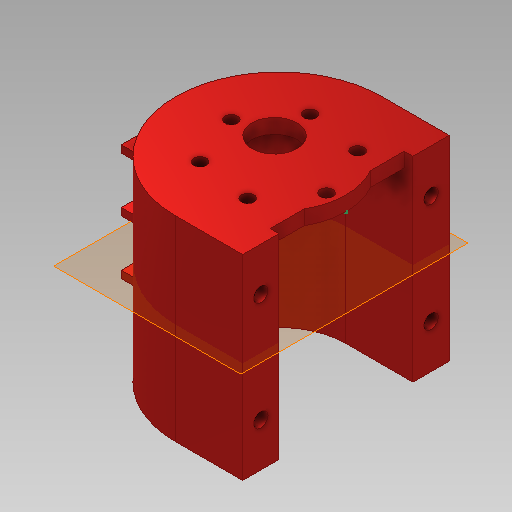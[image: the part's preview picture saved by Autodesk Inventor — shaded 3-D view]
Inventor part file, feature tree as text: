
AUTODESK INVENTOR PART (.ipt)
format: ipt  version: 2020 (Build 240168000, 168)  size: 282,624 bytes
history: native  units: in
note: dims shown in document units (in); Inventor stores cm internally (conversion verified against a paired STEP export)
features: sketch x5, extrude x4, pattern_linear x2, plane x1, mirror x1
ambient origin geometry x8: Origin, YZ Plane, XZ Plane, XY Plane, X Axis, Y Axis, Z Axis, Center Point
bodies: Solid1 (feature_tree)
feature tree (13):
  sketch  "Sketch1"  dims[d2=0.4882in d4=0.2362in]
  extrude  "Extrusion1"  Depth=0.2362in
  extrude  "Extrusion2"  Depth=0.2756in
  sketch  "Sketch2"  dims[d5=3.1496in d13=0.2756in]
  plane  "Work Plane1"
  extrude  "Extrusion3"  Depth=1.4567in
  pattern_linear  "Rectangular Pattern1"  Spacing1=0.3937in  [1 undecoded]
  pattern_linear  "Rectangular Pattern2"  Spacing1=0.1575in  [1 undecoded]
  extrude  "Extrusion4"  Depth=1.9685in TaperAngle=0.0deg
  mirror  "Mirror1"
  sketch  "Sketch7"  dims[d19=0.3937in d20=0.3937in d22=0.1575in d23=0.0in d24=1.9685in d25=0.0in d26=-1.0236in d31=0.3937in d32=0.7874in d33=0.1969in d34=0.1969in d35=0.1181in d36=0.0394in d37=0.1181in d38=0.1181in d39=0.0394in d40=0.1181in d41=0.0394in d42=0.0787in d43=0.0in d44=0.7874in d46=0.5906in d47=0.7874in d49=0.5906in d50=0.1969in d51=0.5906in d52=1.1811in d53=0.1575in d54=0.1575in d55=0.5906in d56=0.0in d58=0.2617in d59=1.2205in d63=1.905in d65=0.7926in d66=0.1378in d67=2.3622in d69=360.0deg]
  sketch  "Sketch5"  dims[d14=0.9606in d17=1.4567in]
  sketch  "Sketch6"  dims[d18=1.122in]
note: 2 required parameter values undecoded (feature->parameter linkage not recoverable at this tier; creation-order binding heuristic only, values carry confidence <= 0.55)
